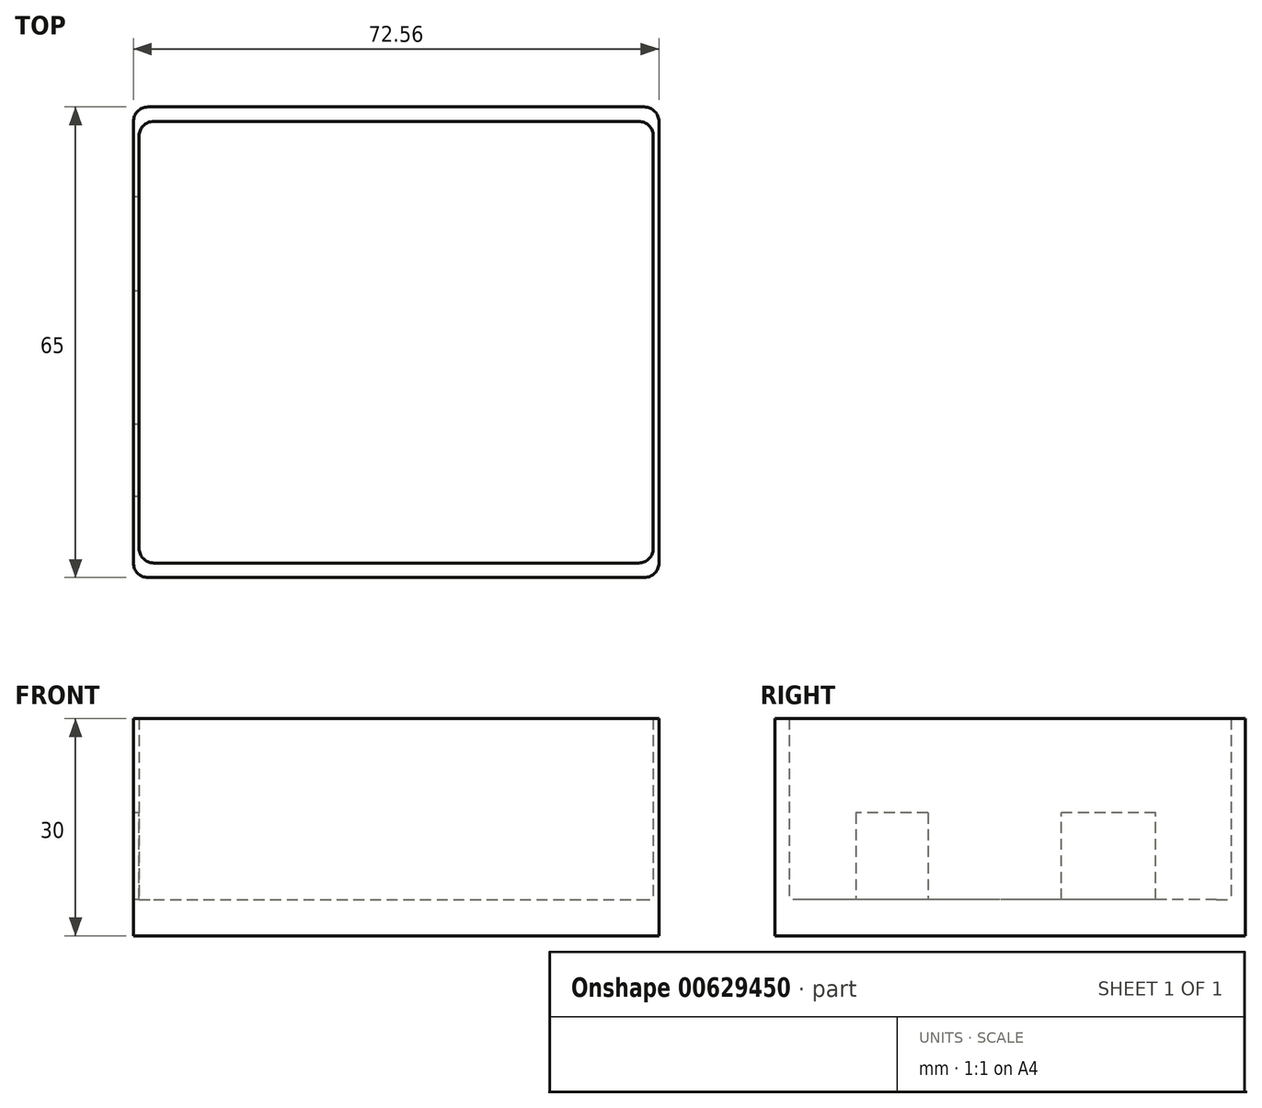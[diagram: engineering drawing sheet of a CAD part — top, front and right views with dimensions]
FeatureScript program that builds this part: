
annotation { "Feature Type Name" : "Feature", "Feature Type Description" : "" }
export const myFeature = defineFeature(function(context is Context, id is Id, definition is map)
    precondition{}
    {
        {
            var Q0;
            Q0=qCreatedBy(makeId("Top.planeOp"),FACE);
            var sketch = newSketch(context, id + "F0", { "sketchPlane" : qUnion([Q0])});
            skLineSegment(sketch, "E0.bottom", {"start": v(-34.28, 32.5) * mm, "end": v(34.28, 32.5) * mm});
            skLineSegment(sketch, "E0.top", {"start": v(-34.28, -32.5) * mm, "end": v(34.28, -32.5) * mm});
            skLineSegment(sketch, "E0.left", {"start": v(-36.28, 30.5) * mm, "end": v(-36.28, -30.5) * mm});
            skLineSegment(sketch, "E0.right", {"start": v(36.28, 30.5) * mm, "end": v(36.28, -30.5) * mm});
            skPoint(sketch, "E0.middle", {"position": v(0, 0) * mm});
            skPoint(sketch, "E1.visualSharp", {"position": v(-36.28, 32.5) * mm});
            skArc(sketch, "E1.filletArc", {"start": v(-34.28, 32.5) * mm, "mid": v(-35.7, 31.91) * mm, "end": v(-36.28, 30.5) * mm});
            skPoint(sketch, "E2.visualSharp", {"position": v(36.28, 32.5) * mm});
            skArc(sketch, "E2.filletArc", {"start": v(36.28, 30.5) * mm, "mid": v(35.7, 31.91) * mm, "end": v(34.28, 32.5) * mm});
            skPoint(sketch, "E3.visualSharp", {"position": v(36.28, -32.5) * mm});
            skArc(sketch, "E3.filletArc", {"start": v(34.28, -32.5) * mm, "mid": v(35.7, -31.91) * mm, "end": v(36.28, -30.5) * mm});
            skPoint(sketch, "E4.visualSharp", {"position": v(-36.28, -32.5) * mm});
            skArc(sketch, "E4.filletArc", {"start": v(-36.28, -30.5) * mm, "mid": v(-35.7, -31.91) * mm, "end": v(-34.28, -32.5) * mm});
            skSolve(sketch);
        }
        {
            var Q0;
            Q0 = qSketchRegion(id + "F0", true);
            extrude(context, id + "F1", {"entities" : qUnion([Q0]), "depth" : 5 * mm, "offsetDistance" : 25 * mm});
        }
        {
            var Q0;
            Q0=makeQuery(id+"F1.opExtrude","CAP_FACE",FACE,{"disambiguationData":[OSD([sQuery(id+"F0.wireOp",EDGE,"E0.bottom"),sQuery(id+"F0.wireOp",EDGE,"E0.top"),sQuery(id+"F0.wireOp",EDGE,"E0.left"),sQuery(id+"F0.wireOp",EDGE,"E0.right"),sQuery(id+"F0.wireOp",EDGE,"E1.filletArc"),sQuery(id+"F0.wireOp",EDGE,"E2.filletArc"),sQuery(id+"F0.wireOp",EDGE,"E3.filletArc"),sQuery(id+"F0.wireOp",EDGE,"E4.filletArc")])],"isStart":false});
            var sketch = newSketch(context, id + "F2", { "sketchPlane" : qUnion([Q0])});
            skLineSegment(sketch, "E5.bottom", {"start": v(-33.5, 30.5) * mm, "end": v(33.5, 30.5) * mm});
            skLineSegment(sketch, "E5.top", {"start": v(-33.5, -30.5) * mm, "end": v(33.5, -30.5) * mm});
            skLineSegment(sketch, "E5.left", {"start": v(-35.5, 28.5) * mm, "end": v(-35.5, -28.5) * mm});
            skLineSegment(sketch, "E5.right", {"start": v(35.5, 28.5) * mm, "end": v(35.5, -28.5) * mm});
            skPoint(sketch, "E5.middle", {"position": v(0, 0) * mm});
            skPoint(sketch, "E6.visualSharp", {"position": v(-35.5, 30.5) * mm});
            skArc(sketch, "E6.filletArc", {"start": v(-33.5, 30.5) * mm, "mid": v(-34.91, 29.91) * mm, "end": v(-35.5, 28.5) * mm});
            skPoint(sketch, "E7.visualSharp", {"position": v(35.5, 30.5) * mm});
            skArc(sketch, "E7.filletArc", {"start": v(35.5, 28.5) * mm, "mid": v(34.91, 29.91) * mm, "end": v(33.5, 30.5) * mm});
            skPoint(sketch, "E8.visualSharp", {"position": v(35.5, -30.5) * mm});
            skArc(sketch, "E8.filletArc", {"start": v(33.5, -30.5) * mm, "mid": v(34.91, -29.91) * mm, "end": v(35.5, -28.5) * mm});
            skPoint(sketch, "E9.visualSharp", {"position": v(-35.5, -30.5) * mm});
            skArc(sketch, "E9.filletArc", {"start": v(-35.5, -28.5) * mm, "mid": v(-34.91, -29.91) * mm, "end": v(-33.5, -30.5) * mm});
            skPoint(sketch, "E10.cornerSnap0", {"position": v(-32.87, 29.09) * mm});
            skPoint(sketch, "E11.visualSharp", {"position": v(38.41, 35.88) * mm});
            skPoint(sketch, "E12.visualSharp", {"position": v(36.28, -29.09) * mm});
            skPoint(sketch, "E13.visualSharp", {"position": v(-38.41, -35.88) * mm});
            skPoint(sketch, "E14.visualSharp", {"position": v(-36.28, 29.09) * mm});
            skSolve(sketch);
        }
        {
            var Q0;
            Q0=makeQuery(id+"F2.imprint","IMPRINT",FACE,{"disambiguationData":[TD([[makeQuery(id+"F2.imprint","IMPRINT",EDGE,{"derivedFrom":sQuery(id+"F2.wireOp",EDGE,"E5.bottom")}),1.0]])]});
            extrude(context, id + "F3", {"entities" : qUnion([Q0]), "operationType" : NewBodyOperationType.ADD, "depth" : 25 * mm, "offsetDistance" : 25 * mm});
        }
        {
            var Q0;
            Q0=makeQuery(id+"F3.boolean.opBoolean","MERGE",FACE,{"derivedFrom":[makeQuery(id+"F1.opExtrude","SWEPT_FACE",FACE,{"disambiguationData":[OSD([sQuery(id+"F0.wireOp",EDGE,"E0.left")])]}),makeQuery(id+"F3.opExtrude","SWEPT_FACE",FACE,{"disambiguationData":[OSD([sQuery(id+"F2.wireOp",EDGE,"E10.left")])]})]});
            var sketch = newSketch(context, id + "F4", { "sketchPlane" : qUnion([Q0])});
            skLineSegment(sketch, "E15.bottom", {"start": v(-20.07, 5) * mm, "end": v(-7.07, 5) * mm});
            skLineSegment(sketch, "E15.top", {"start": v(-20.07, 17) * mm, "end": v(-7.07, 17) * mm});
            skLineSegment(sketch, "E15.left", {"start": v(-20.07, 5) * mm, "end": v(-20.07, 17) * mm});
            skLineSegment(sketch, "E15.right", {"start": v(-7.07, 5) * mm, "end": v(-7.07, 17) * mm});
            skLineSegment(sketch, "E16.bottom", {"start": v(11.33, 17) * mm, "end": v(21.33, 17) * mm});
            skLineSegment(sketch, "E16.top", {"start": v(11.33, 5) * mm, "end": v(21.33, 5) * mm});
            skLineSegment(sketch, "E16.left", {"start": v(11.33, 17) * mm, "end": v(11.33, 5) * mm});
            skLineSegment(sketch, "E16.right", {"start": v(21.33, 17) * mm, "end": v(21.33, 5) * mm});
            skSolve(sketch);
        }
        {
            var Q0;
            Q0=makeQuery(id+"F4.imprint","IMPRINT",FACE,{"disambiguationData":[TD([[makeQuery(id+"F4.imprint","IMPRINT",EDGE,{"derivedFrom":sQuery(id+"F4.wireOp",EDGE,"E16.bottom")}),-1.0]])]});
            var Q1;
            Q1=makeQuery(id+"F4.imprint","IMPRINT",FACE,{"disambiguationData":[TD([[makeQuery(id+"F4.imprint","IMPRINT",EDGE,{"derivedFrom":sQuery(id+"F4.wireOp",EDGE,"E15.bottom")}),1.0]])]});
            extrude(context, id + "F5", {"entities" : qUnion([Q0, Q1]), "operationType" : NewBodyOperationType.REMOVE, "depth" : -2.1 * mm, "offsetDistance" : 25 * mm});
        }
    });
